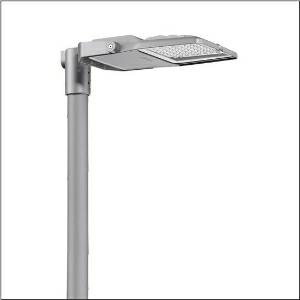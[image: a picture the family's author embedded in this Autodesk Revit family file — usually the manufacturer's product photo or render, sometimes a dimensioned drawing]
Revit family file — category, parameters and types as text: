
# Revit family: floodlight_fl_21_mini___pl43_5xa7776c2a3a_c8bd
name_source: partatom
category: Lighting Fixtures
units: mm (PartAtom-declared; Revit-internal decimal feet)

## family parameters
Cut with Voids When Loaded = No
Host = Face
Light Source = No
Part Type = Normal
Room Calculation Point = No
Round Connector Dimension = Use Diameter
Shared = No

## types (1)
- --- (1 x LED, 12500 lm, 89 W, 3000K)
    Apparent Load = 89 VA
    CIE Flux Codes = 27 78 99 100 100
    Color Rendering = 70
    Color Temperature = 3000K
    Default Elevation = 1800 mm
    Description = Floodlight FL 21 mini, floodlight, primary light control with lens, of PMMA, primary optical cover: protective disc, of toughened safety glass, transparent, light distribution: PL43, light emission: direct distribution, installation type: surface-mounted, LED, High Power LED, rated luminous flux: 12.500lm, luminous efficacy: 140lm/W, light colour: 730, colour temperature: 3000K, control gear: ECG Smart Interface, control: flexible luminous flux parameterisation, time-dependent luminous flux control, constant luminous flux control, overheat protection, presetting dimming logarithmic, with terminal, 6-pole, mains connection: 220..240V, AC, 50/60Hz, start of lifetime: 89W, end of lifetime: 94W, reduction: 43W, luminaire housing, of diecast aluminium, powder-coated, Siteco® metallic grey (DB 702S), corrosivity category C5 according to DIN EN ISO 12944, mast bracket, of steel, galvanised, powder-coated, Siteco® metallic grey (DB 702S), protection rating (complete): IP66, insulation class (complete): insulation class II (safety insulation), certification: CE, protection symbol: D, impact resistance: IK08, permissible operating ambient temperature: -40..+40°C, permissible operating ambient temperature for outdoor applications: -40..+50°C, standard: DIN EN 12944, packaging unit: 1 piece

Light Distribution: PL43
    Height = 70 mm
    Lamp = 1 x LED
    Lamp Light Flux = 12500 lm
    Lamp Power = 89 W
    Lamp count = 1
    Length = 485 mm
    Luminous efficacy = 140 lm/W
    Manufacturer = Siteco
    ModVariant = No
    Model = 5XA7776C2A3A
    Number of Poles = 1
    OnlyDefault = Yes
    Power Factor = 1
    Product Name = Floodlight FL 21 mini | PL43
    Product group = floodlight | pylon top
    ProductGroupID = 6101
    Protection Class = Protection class II
    Protection Degree = IP 66
    RLX_Detail_Level = 1
    RlxData = <blob elided: 100577 chars, md5=9ddf34e7>
    Socket = socket
    Standby Power = 0 W
    System Light Flux = 12500 lm
    System Power = 89 W
    Type Comments = factory setting: luminous flux: 100 % | dim-lin: 254 | 456 mA
    Type Image = l_1007125.jpg
    URL = http://relux.com
    VarID = @adj_072351
    Voltage = 0 V
    Weight = 0.00 kg
    Width = 337 mm

## geometry (parser evidence)
native form markers: Blend x4, Sweep x13
no freeform markers — native parametric forms only
